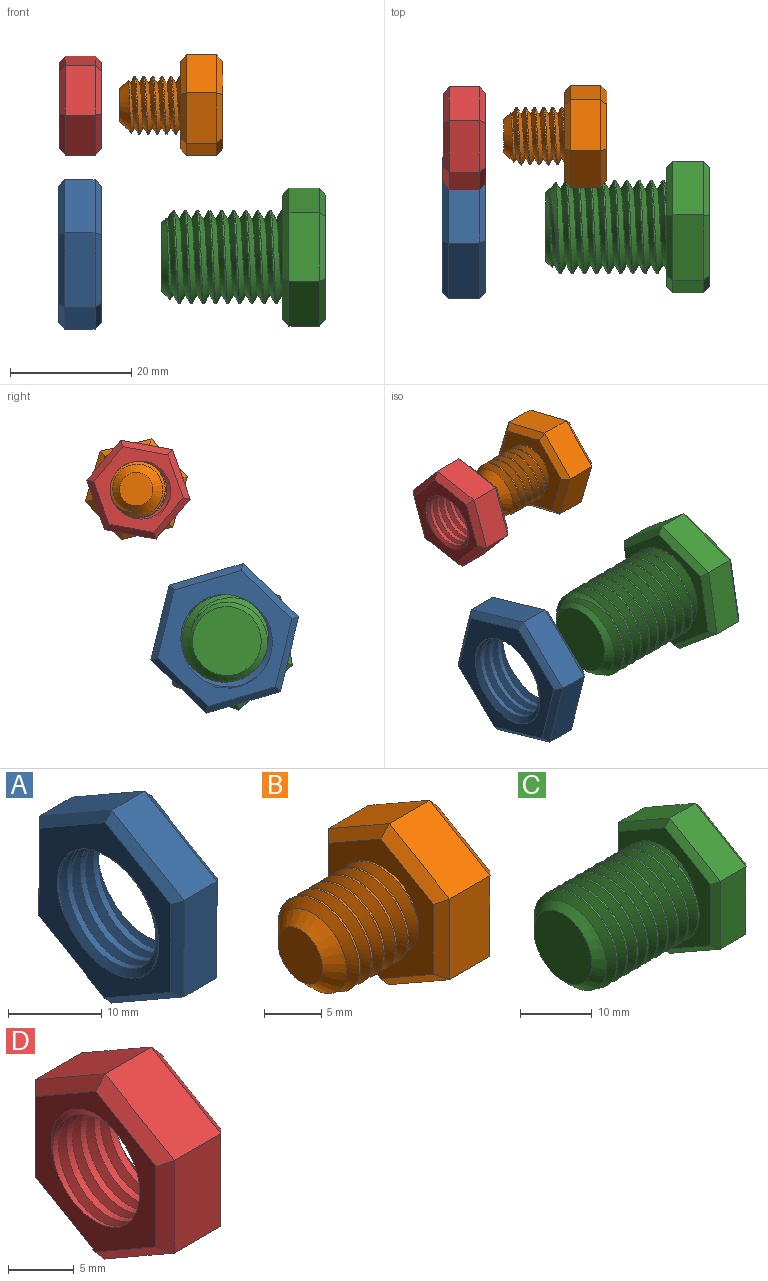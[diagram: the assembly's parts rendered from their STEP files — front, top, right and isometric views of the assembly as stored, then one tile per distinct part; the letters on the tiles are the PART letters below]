
ASSEMBLY  parts=4 mates=2
PART A: 24 faces, bbox 8.7x22.5x25.9 mm
  f0: cylinder r=7.24mm len=14.48mm, axis (1,0,0), area 123.5mm2, adj f7,f8,f22,f23
  f1: plane 10.98x6.38mm, normal (0,-0.5,0.86), area 63.5mm2, adj f2,f6,f14,f18
  f2: plane 12.7x5mm, normal (0,-1,0), area 63.5mm2, adj f1,f3,f12,f16
  f3: plane 11.02x6.32mm, normal (0,-0.5,-0.87), area 63.5mm2, adj f2,f4,f10,f15
  f4: plane 10.98x6.38mm, normal (0,0.5,-0.86), area 63.5mm2, adj f3,f5,f9,f17
  f5: plane 12.7x5mm, normal (0,1,0), area 63.5mm2, adj f4,f6,f11,f19
  f6: plane 11.02x6.32mm, normal (0,0.5,0.87), area 63.5mm2, adj f1,f5,f13,f20
  f7: plane 23.54x20.48mm, normal (-1,0,0), area 165.1mm2, adj f0,f9,f10,f11,f12,f13,f14,f21
  f8: plane 23.54x20.48mm, normal (1,0,0), area 165.1mm2, adj f0,f15,f16,f17,f18,f19,f20,f21
  f9: plane 10.99x6.96mm, normal (-0.71,0.36,-0.61), area 17.1mm2, adj f4,f7,f10,f11
  f10: plane 11.02x6.9mm, normal (-0.71,-0.35,-0.61), area 17.1mm2, adj f3,f7,f9,f12
  f11: plane 12.7x1.03mm, normal (-0.71,0.71,0), area 17.1mm2, adj f5,f7,f9,f13
  f12: plane 12.7x1.03mm, normal (-0.71,-0.71,0), area 17.1mm2, adj f2,f7,f10,f14
  f13: plane 11.02x6.9mm, normal (-0.71,0.35,0.61), area 17.1mm2, adj f6,f7,f11,f14
  f14: plane 10.99x6.96mm, normal (-0.71,-0.36,0.61), area 17.1mm2, adj f1,f7,f12,f13
  f15: plane 11.02x6.9mm, normal (0.71,-0.35,-0.61), area 17.1mm2, adj f3,f8,f16,f17
  f16: plane 12.7x1.03mm, normal (0.71,-0.71,0), area 17.1mm2, adj f2,f8,f15,f18
  f17: plane 10.99x6.96mm, normal (0.71,0.36,-0.61), area 17.1mm2, adj f4,f8,f15,f19
  f18: plane 10.99x6.96mm, normal (0.71,-0.36,0.61), area 17.1mm2, adj f1,f8,f16,f20
  f19: plane 12.7x1.03mm, normal (0.71,0.71,0), area 17.1mm2, adj f5,f8,f17,f20
  f20: plane 11.02x6.9mm, normal (0.71,0.35,0.61), area 17.1mm2, adj f6,f8,f18,f19
  f21: bspline ~19.18x16.61mm, area 49.1mm2, adj f7,f8,f22,f23
  f22: bspline ~18.94x16.4mm, area 183.8mm2, adj f0,f7,f8,f21
  f23: bspline ~18.92x16.39mm, area 183.8mm2, adj f0,f7,f8,f21
PART B: 25 faces, bbox 17.8x15.9x18.1 mm
  f0: cylinder r=4.75mm len=9.5mm, axis (1,0,0), area 28.1mm2, adj f1,f2,f4,f12
  f1: bspline ~10.97x9.91mm, area 196.7mm2, adj f0,f2,f4,f12
  f2: bspline ~10.97x10.66mm, area 196.6mm2, adj f0,f1,f4,f12
  f3: plane 5.5x5.5mm, normal (-1,0,0), area 23.8mm2, adj f4
  f4: cone r=4.75mm half-angle=45deg, axis (1,0,0), area 47.4mm2, adj f0,f1,f2,f3
  f5: plane 7.48x5mm, normal (0,-0.5,0.86), area 43.3mm2, adj f6,f10,f18,f22
  f6: plane 8.66x5mm, normal (0,-1,0), area 43.3mm2, adj f5,f7,f16,f20
  f7: plane 7.52x5mm, normal (0,-0.5,-0.87), area 43.3mm2, adj f6,f8,f14,f19
  f8: plane 7.48x5mm, normal (0,0.5,-0.86), area 43.3mm2, adj f7,f9,f13,f21
  f9: plane 8.66x5mm, normal (0,1,0), area 43.3mm2, adj f8,f10,f15,f23
  f10: plane 7.52x5mm, normal (0,0.5,0.87), area 43.3mm2, adj f5,f9,f17,f24
  f11: plane 15.01x13.03mm, normal (1,0,0), area 146.4mm2, adj f13,f14,f15,f16,f17,f18
  f12: plane 15.83x13.85mm, normal (-1,0,0), area 89.2mm2, adj f0,f1,f2,f19,f20,f21,f22,f23
  f13: plane 7.49x4.93mm, normal (0.71,0.36,-0.61), area 11.4mm2, adj f8,f11,f14,f15
  f14: plane 7.52x4.88mm, normal (0.71,-0.35,-0.61), area 11.4mm2, adj f7,f11,f13,f16
  f15: plane 8.66x1.03mm, normal (0.71,0.71,0), area 11.4mm2, adj f9,f11,f13,f17
  f16: plane 8.66x1.03mm, normal (0.71,-0.71,0), area 11.4mm2, adj f6,f11,f14,f18
  f17: plane 7.52x4.88mm, normal (0.71,0.35,0.61), area 11.4mm2, adj f10,f11,f15,f18
  f18: plane 7.49x4.93mm, normal (0.71,-0.36,0.61), area 11.4mm2, adj f5,f11,f16,f17
  f19: plane 7.52x4.88mm, normal (-0.71,-0.35,-0.61), area 11.4mm2, adj f7,f12,f20,f21
  f20: plane 8.66x1.03mm, normal (-0.71,-0.71,0), area 11.4mm2, adj f6,f12,f19,f22
  f21: plane 7.49x4.93mm, normal (-0.71,0.36,-0.61), area 11.4mm2, adj f8,f12,f19,f23
  f22: plane 7.49x4.93mm, normal (-0.71,-0.36,0.61), area 11.4mm2, adj f5,f12,f20,f24
  f23: plane 8.66x1.03mm, normal (-0.71,0.71,0), area 11.4mm2, adj f9,f12,f21,f24
  f24: plane 7.52x4.88mm, normal (-0.71,0.35,0.61), area 11.4mm2, adj f10,f12,f22,f23
PART C: 26 faces, bbox 27.7x20x23.1 mm
  f0: cylinder r=7.68mm len=18mm, axis (1,0,0), area 139.1mm2, adj f1,f2,f5,f13
  f1: bspline ~20.88x17.74mm, area 713.8mm2, adj f0,f2,f4,f5,f13
  f2: bspline ~21.88x17.74mm, area 715.1mm2, adj f0,f1,f4,f5,f13
  f3: plane 11.36x11.36mm, normal (-1,0,0), area 101.4mm2, adj f4
  f4: cone r=7.68mm half-angle=45deg, axis (1,0,0), area 63.2mm2, adj f1,f2,f3,f5
  f5: cone r=7.68mm half-angle=45deg, axis (1,0,0), area 13.2mm2, adj f0,f1,f2,f4
  f6: plane 9.98x5.81mm, normal (0,-0.5,0.86), area 57.7mm2, adj f7,f11,f19,f23
  f7: plane 11.55x5mm, normal (0,-1,0), area 57.7mm2, adj f6,f8,f17,f21
  f8: plane 10.02x5.74mm, normal (0,-0.5,-0.87), area 57.7mm2, adj f7,f9,f15,f20
  f9: plane 9.98x5.81mm, normal (0,0.5,-0.86), area 57.7mm2, adj f8,f10,f14,f22
  f10: plane 11.55x5mm, normal (0,1,0), area 57.7mm2, adj f9,f11,f16,f24
  f11: plane 10.02x5.74mm, normal (0,0.5,0.87), area 57.7mm2, adj f6,f10,f18,f25
  f12: plane 20.78x18.04mm, normal (1,0,0), area 280.6mm2, adj f14,f15,f16,f17,f18,f19
  f13: plane 20.78x18.04mm, normal (-1,0,0), area 125.2mm2, adj f0,f1,f2,f20,f21,f22,f23,f24
  f14: plane 9.98x6.38mm, normal (0.71,0.36,-0.61), area 15.5mm2, adj f9,f12,f15,f16
  f15: plane 10.02x6.32mm, normal (0.71,-0.35,-0.61), area 15.5mm2, adj f8,f12,f14,f17
  f16: plane 11.55x1.04mm, normal (0.71,0.71,0), area 15.5mm2, adj f10,f12,f14,f18
  f17: plane 11.55x1.04mm, normal (0.71,-0.71,0), area 15.5mm2, adj f7,f12,f15,f19
  f18: plane 10.02x6.32mm, normal (0.71,0.35,0.61), area 15.5mm2, adj f11,f12,f16,f19
  f19: plane 9.98x6.38mm, normal (0.71,-0.36,0.61), area 15.5mm2, adj f6,f12,f17,f18
  f20: plane 10.02x6.32mm, normal (-0.71,-0.35,-0.61), area 15.5mm2, adj f8,f13,f21,f22
  f21: plane 11.55x1.04mm, normal (-0.71,-0.71,0), area 15.5mm2, adj f7,f13,f20,f23
  f22: plane 9.98x6.38mm, normal (-0.71,0.36,-0.61), area 15.5mm2, adj f9,f13,f20,f24
  f23: plane 9.98x6.38mm, normal (-0.71,-0.36,0.61), area 15.5mm2, adj f6,f13,f21,f25
  f24: plane 11.55x1.04mm, normal (-0.71,0.71,0), area 15.5mm2, adj f10,f13,f22,f25
  f25: plane 10.02x6.32mm, normal (-0.71,0.35,0.61), area 15.5mm2, adj f11,f13,f23,f24
PART D: 23 faces, bbox 9.1x15.4x17.7 mm
  f0: plane 7.49x5mm, normal (0,-0.5,0.86), area 43.3mm2, adj f1,f5,f13,f17
  f1: plane 8.66x5mm, normal (0,-1,0), area 43.3mm2, adj f0,f2,f11,f15
  f2: plane 7.51x5mm, normal (0,-0.5,-0.87), area 43.3mm2, adj f1,f3,f9,f14
  f3: plane 7.49x5mm, normal (0,0.5,-0.86), area 43.3mm2, adj f2,f4,f8,f16
  f4: plane 8.66x5mm, normal (0,1,0), area 43.3mm2, adj f3,f5,f10,f18
  f5: plane 7.51x5mm, normal (0,0.5,0.87), area 43.3mm2, adj f0,f4,f12,f19
  f6: plane 15.37x13.38mm, normal (-1,0,0), area 71.4mm2, adj f8,f9,f10,f11,f12,f13,f20,f21
  f7: plane 15.37x13.38mm, normal (1,0,0), area 71.4mm2, adj f14,f15,f16,f17,f18,f19,f20,f21
  f8: plane 7.49x4.93mm, normal (-0.71,0.36,-0.61), area 11.4mm2, adj f3,f6,f9,f10
  f9: plane 7.51x4.89mm, normal (-0.71,-0.35,-0.61), area 11.4mm2, adj f2,f6,f8,f11
  f10: plane 8.66x1.02mm, normal (-0.71,0.71,0), area 11.4mm2, adj f4,f6,f8,f12
  f11: plane 8.66x1.02mm, normal (-0.71,-0.71,0), area 11.4mm2, adj f1,f6,f9,f13
  f12: plane 7.51x4.89mm, normal (-0.71,0.35,0.61), area 11.4mm2, adj f5,f6,f10,f13
  f13: plane 7.49x4.93mm, normal (-0.71,-0.36,0.61), area 11.4mm2, adj f0,f6,f11,f12
  f14: plane 7.51x4.89mm, normal (0.71,-0.35,-0.61), area 11.4mm2, adj f2,f7,f15,f16
  f15: plane 8.66x1.02mm, normal (0.71,-0.71,0), area 11.4mm2, adj f1,f7,f14,f17
  f16: plane 7.49x4.93mm, normal (0.71,0.36,-0.61), area 11.4mm2, adj f3,f7,f14,f18
  f17: plane 7.49x4.93mm, normal (0.71,-0.36,0.61), area 11.4mm2, adj f0,f7,f15,f19
  f18: plane 8.66x1.02mm, normal (0.71,0.71,0), area 11.4mm2, adj f4,f7,f16,f19
  f19: plane 7.51x4.89mm, normal (0.71,0.35,0.61), area 11.4mm2, adj f5,f7,f17,f18
  f20: cylinder r=4.66mm len=9.32mm, axis (1,0,0), area 85.4mm2, adj f6,f7,f21,f22
  f21: bspline ~12.5x10.82mm, area 128.4mm2, adj f6,f7,f20,f22
  f22: bspline ~12.5x10.82mm, area 128.5mm2, adj f6,f7,f20,f21
PLACE A rot(axis=(0,0.6,-0.8),180deg) t=(-55.27,-6.86,23.48)mm fixed
PLACE B rot(axis=(-1,0,0),43.8deg) t=(-31.66,7.73,48.08)mm
PLACE C rot(axis=(1,0,0),109.9deg) t=(-14.77,-7.19,23.03)mm
PLACE D rot(axis=(1,0,0),100.2deg) t=(-48.16,7.38,48.02)mm fixed
MATE cylindrical C.f0 <-> A.f7  axis (-1,0,0) through (-38.27,-7.19,23.03)mm
MATE cylindrical B.f0 <-> D.f6  axis (-1,0,0) through (-45.16,7.73,48.08)mm
